FCSTD DOCUMENT  (FreeCAD 0.17R13509 (Git))
Label: Beam
License: All rights reserved
LicenseURL: http://en.wikipedia.org/wiki/All_rights_reserved
objects: Sketcher::SketchObject×1, PartDesign::Body×1, PartDesign::Pad×1
note: 4 computed .brp shape members not serialized (recipe doc carries the construction recipe); baked Part::Feature solids carry a one-line shape summary decoded from their .brp

FEATURE [Sketcher::SketchObject] Sketch
  MapMode = 5
  Support = -> [XY_Plane]
  sketch-geometry (22):
    g0: LineSegment StartX=-53 StartY=6 StartZ=0 EndX=53 EndY=6 EndZ=0
    g1: LineSegment [constr] StartX=53 StartY=6 StartZ=0 EndX=53 EndY=-6 EndZ=0
    g2: LineSegment StartX=53 StartY=-6 StartZ=0 EndX=-53 EndY=-6 EndZ=0
    g3: LineSegment [constr] StartX=-53 StartY=-6 StartZ=0 EndX=-53 EndY=6 EndZ=0
    g4: LineSegment StartX=53 StartY=6 StartZ=0 EndX=53 EndY=2 EndZ=0
    g5: LineSegment StartX=53 StartY=2 StartZ=0 EndX=42 EndY=2 EndZ=0
    g6: LineSegment StartX=42 StartY=2 StartZ=0 EndX=42 EndY=-2 EndZ=0
    g7: LineSegment StartX=42 StartY=-2 StartZ=0 EndX=53 EndY=-2 EndZ=0
    g8: LineSegment StartX=53 StartY=-2 StartZ=0 EndX=53 EndY=-6 EndZ=0
    g9: LineSegment StartX=-53 StartY=6 StartZ=0 EndX=-53 EndY=2 EndZ=0
    g10: LineSegment StartX=-53 StartY=2 StartZ=0 EndX=-42 EndY=2 EndZ=0
    g11: LineSegment StartX=-42 StartY=2 StartZ=0 EndX=-42 EndY=-2 EndZ=0
    g12: LineSegment StartX=-42 StartY=-2 StartZ=0 EndX=-53 EndY=-2 EndZ=0
    g13: LineSegment StartX=-53 StartY=-2 StartZ=0 EndX=-53 EndY=-6 EndZ=0
    g14: LineSegment StartX=-39 StartY=2.5 StartZ=0 EndX=-37 EndY=2.5 EndZ=0
    g15: LineSegment StartX=-37 StartY=2.5 StartZ=0 EndX=-37 EndY=-2.5 EndZ=0
    g16: LineSegment StartX=-37 StartY=-2.5 StartZ=0 EndX=-39 EndY=-2.5 EndZ=0
    g17: LineSegment StartX=-39 StartY=-2.5 StartZ=0 EndX=-39 EndY=2.5 EndZ=0
    g18: LineSegment StartX=37 StartY=2.5 StartZ=0 EndX=39 EndY=2.5 EndZ=0
    g19: LineSegment StartX=39 StartY=2.5 StartZ=0 EndX=39 EndY=-2.5 EndZ=0
    g20: LineSegment StartX=39 StartY=-2.5 StartZ=0 EndX=37 EndY=-2.5 EndZ=0
    g21: LineSegment StartX=37 StartY=-2.5 StartZ=0 EndX=37 EndY=2.5 EndZ=0
  constraints (65):
    c: Coincident(g0,g1)
    c: Coincident(g1,g2)
    c: Coincident(g2,g3)
    c: Coincident(g3,g0)
    c: Horizontal(g0)
    c: Horizontal(g2)
    c: Vertical(g3)
    c: DistanceX(g2,g2) = 106
    c: DistanceY(g1,g1) = 12
    c: Symmetric(g2,g0,g-1)
    c: Symmetric(g0,g0,g-2)
    c: Coincident(g4,g0)
    c: PointOnObject(g4,g1)
    c: Vertical(g4)
    c: Coincident(g5,g4)
    c: Horizontal(g5)
    c: Coincident(g5,g6)
    c: Vertical(g6)
    c: Coincident(g6,g7)
    c: PointOnObject(g7,g1)
    c: Horizontal(g7)
    c: Coincident(g7,g8)
    c: Coincident(g8,g1)
    c: Equal(g6,g4)
    c: Equal(g4,g8)
    c: DistanceX(g5,g5) = 11
    c: Coincident(g0,g9)
    c: PointOnObject(g9,g3)
    c: Coincident(g9,g10)
    c: Coincident(g10,g11)
    c: Vertical(g11)
    c: Coincident(g11,g12)
    c: PointOnObject(g12,g3)
    c: Horizontal(g12)
    c: Coincident(g12,g13)
    c: Coincident(g13,g2)
    c: Horizontal(g10)
    c: Equal(g11,g9)
    c: Equal(g9,g13)
    c: Equal(g10,g5)
    c: Coincident(g14,g15)
    c: Coincident(g15,g16)
    c: Coincident(g16,g17)
    c: Coincident(g17,g14)
    c: Horizontal(g14)
    c: Horizontal(g16)
    c: Vertical(g15)
    c: Vertical(g17)
    c: Symmetric(g14,g16,g-1)
    c: DistanceX(g14,g14) = 2
    c: DistanceY(g15,g15) = 5
    c: DistanceX(g10,g14) = 3
    c: Coincident(g18,g19)
    c: Coincident(g19,g20)
    c: Coincident(g20,g21)
    c: Coincident(g21,g18)
    c: Horizontal(g18)
    c: Horizontal(g20)
    c: Vertical(g19)
    c: Vertical(g21)
    c: Symmetric(g18,g20,g-1)
    c: DistanceX(g18,g5) = 3
    c: Equal(g21,g15)
    c: Equal(g18,g14)
    c: DistanceX(g11,g20) = 79
FEATURE [PartDesign::Body] Body
  Group = -> [Sketch]
  Origin = -> Origin
FEATURE [PartDesign::Pad] Pad
  Length = 3
  Length2 = 100
  Midplane = true
  Profile = -> Sketch
  Refine = true
  Type = 0
